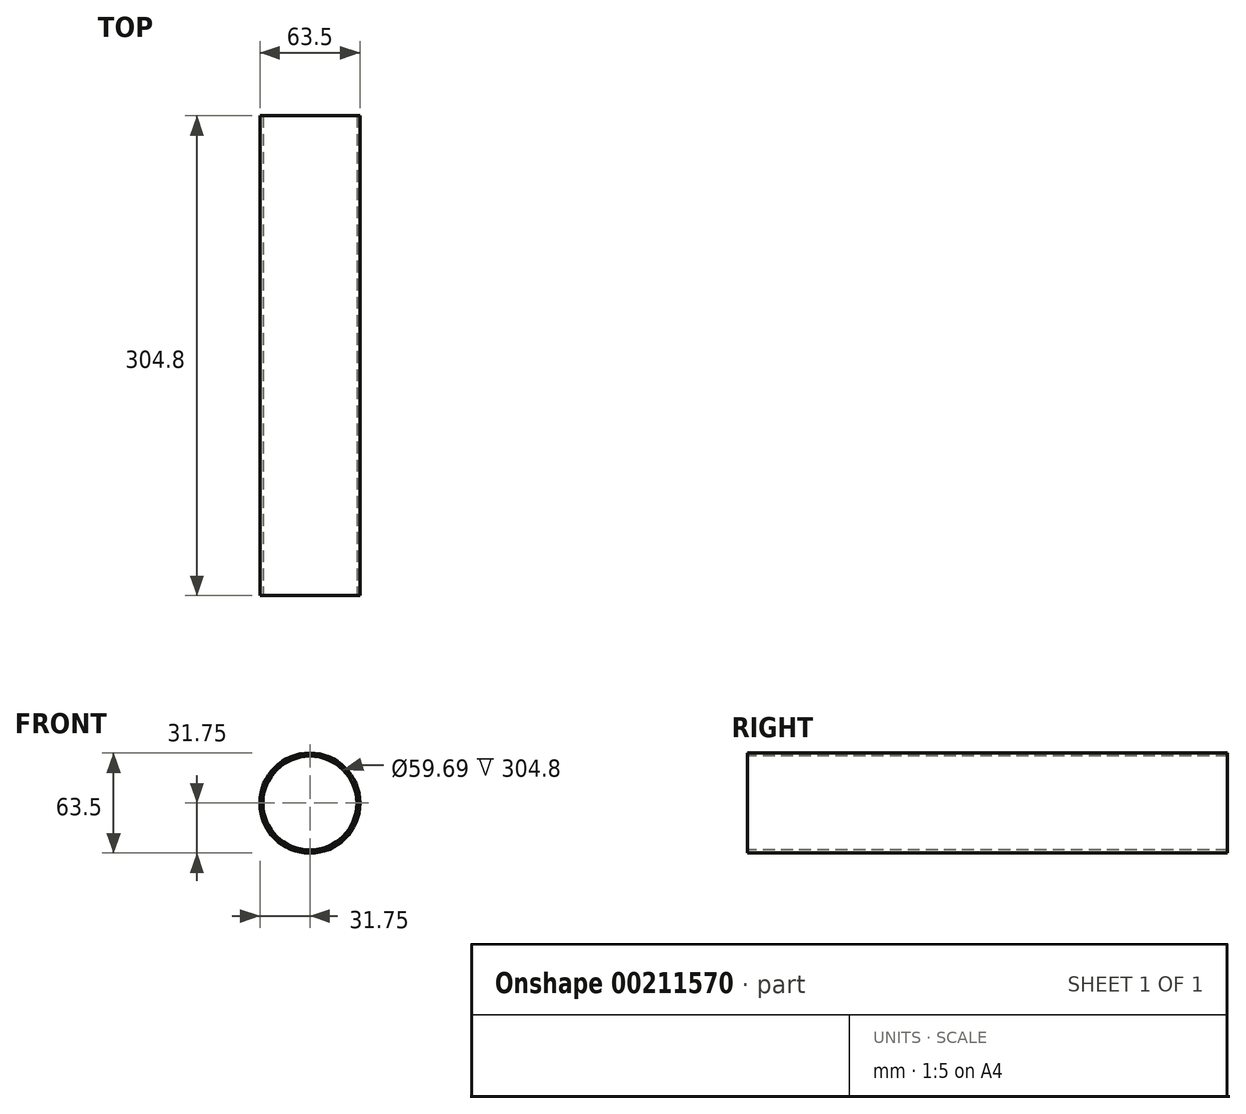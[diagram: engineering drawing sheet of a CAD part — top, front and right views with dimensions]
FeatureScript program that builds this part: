
annotation { "Feature Type Name" : "Feature", "Feature Type Description" : "" }
export const myFeature = defineFeature(function(context is Context, id is Id, definition is map)
    precondition{}
    {
        {
            var Q0;
            Q0=qCreatedBy(makeId("Front.planeOp"),FACE);
            var sketch = newSketch(context, id + "F0", { "sketchPlane" : qUnion([Q0])});
            skCircle(sketch, "E0", {"center": v(0, 0) * mm, "radius": 31.75 * mm});
            skSolve(sketch);
        }
        {
            var Q0;
            Q0=makeQuery(id+"F0.imprint","IMPRINT",FACE,{"disambiguationData":[TD([[makeQuery(id+"F0.imprint","IMPRINT",EDGE,{"derivedFrom":sQuery(id+"F0.wireOp",EDGE,"E0")}),1.0]])]});
            extrude(context, id + "F1", {"entities" : qUnion([Q0]), "oppositeDirection" : true, "depth" : 304.8 * mm});
        }
        {
            var Q0;
            Q0=qCreatedBy(makeId("Front.planeOp"),FACE);
            var sketch = newSketch(context, id + "F2", { "sketchPlane" : qUnion([Q0])});
            skCircle(sketch, "E1", {"center": v(0, 0) * mm, "radius": 29.85 * mm});
            skSolve(sketch);
        }
        {
            var Q0;
            Q0 = qSketchRegion(id + "F2", true);
            var Q1;
            Q1=makeQuery(id+"F2.imprint","IMPRINT",FACE,{"disambiguationData":[TD([[makeQuery(id+"F2.imprint","IMPRINT",EDGE,{"derivedFrom":sQuery(id+"F2.wireOp",EDGE,"E1")}),1.0]])]});
            extrude(context, id + "F3", {"entities" : qUnion([Q0, Q1]), "operationType" : NewBodyOperationType.REMOVE, "oppositeDirection" : true, "depth" : 304.8 * mm});
        }
    });
